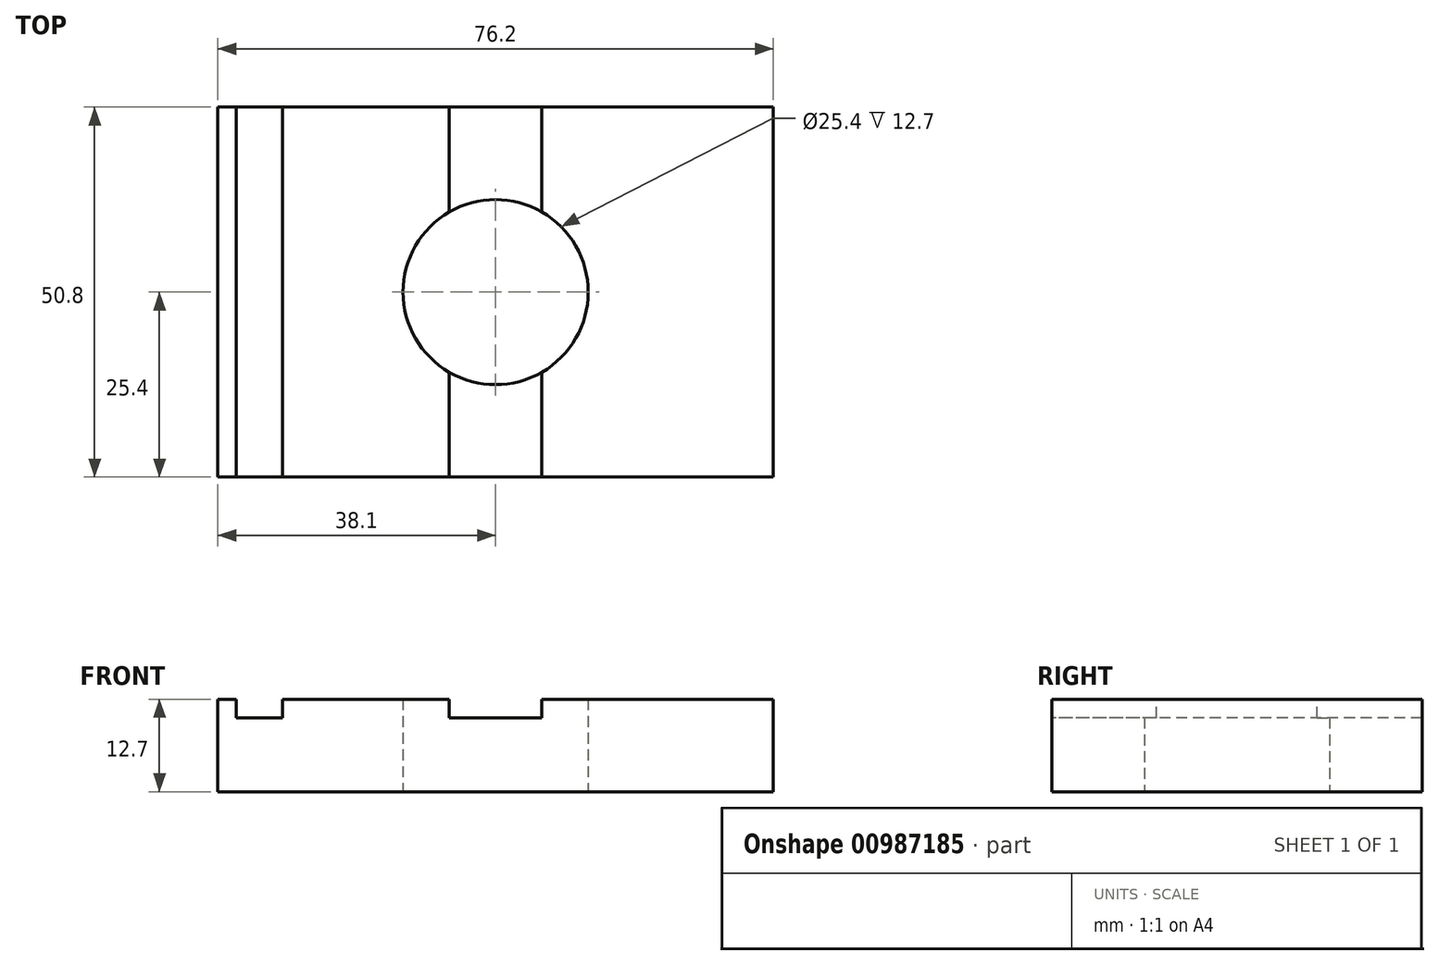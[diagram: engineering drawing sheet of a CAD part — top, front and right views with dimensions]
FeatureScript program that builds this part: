
annotation { "Feature Type Name" : "Feature", "Feature Type Description" : "" }
export const myFeature = defineFeature(function(context is Context, id is Id, definition is map)
    precondition{}
    {
        {
            var Q0;
            Q0=qCreatedBy(makeId("Top.planeOp"),FACE);
            var sketch = newSketch(context, id + "F0", { "sketchPlane" : qUnion([Q0])});
            skLineSegment(sketch, "E0.bottom", {"start": v(-38.1, 25.4) * mm, "end": v(38.1, 25.4) * mm});
            skLineSegment(sketch, "E0.top", {"start": v(-38.1, -25.4) * mm, "end": v(38.1, -25.4) * mm});
            skLineSegment(sketch, "E0.left", {"start": v(-38.1, 25.4) * mm, "end": v(-38.1, -25.4) * mm});
            skLineSegment(sketch, "E0.right", {"start": v(38.1, 25.4) * mm, "end": v(38.1, -25.4) * mm});
            skPoint(sketch, "E0.middle", {"position": v(0, 0) * mm});
            skCircle(sketch, "E1", {"center": v(0, 0) * mm, "radius": 12.7 * mm});
            skSolve(sketch);
        }
        {
            var Q0;
            Q0=makeQuery(id+"F0.imprint","IMPRINT",FACE,{"disambiguationData":[TD([[makeQuery(id+"F0.imprint","IMPRINT",EDGE,{"derivedFrom":sQuery(id+"F0.wireOp",EDGE,"E0.bottom")}),-1.0]])]});
            extrude(context, id + "F1", {"entities" : qUnion([Q0]), "depth" : 12.7 * mm, "offsetDistance" : 25.4 * mm});
        }
        {
            var Q0;
            Q0=makeQuery(id+"F1.opExtrude","CAP_FACE",FACE,{"disambiguationData":[OSD([sQuery(id+"F0.wireOp",EDGE,"E0.bottom"),sQuery(id+"F0.wireOp",EDGE,"E0.top"),sQuery(id+"F0.wireOp",EDGE,"E0.left"),sQuery(id+"F0.wireOp",EDGE,"E0.right"),sQuery(id+"F0.wireOp",EDGE,"E1")])],"isStart":false});
            var sketch = newSketch(context, id + "F2", { "sketchPlane" : qUnion([Q0])});
            skLineSegment(sketch, "E2.bottom", {"start": v(-35.56, 25.4) * mm, "end": v(-29.2, 25.4) * mm});
            skLineSegment(sketch, "E2.top", {"start": v(-35.56, -25.4) * mm, "end": v(-29.2, -25.4) * mm});
            skLineSegment(sketch, "E2.left", {"start": v(-35.56, 25.4) * mm, "end": v(-35.56, -25.4) * mm});
            skLineSegment(sketch, "E2.right", {"start": v(-29.2, 25.4) * mm, "end": v(-29.2, -25.4) * mm});
            skLineSegment(sketch, "E3.bottom", {"start": v(-6.35, 25.4) * mm, "end": v(6.35, 25.4) * mm});
            skLineSegment(sketch, "E3.top", {"start": v(-6.35, -25.4) * mm, "end": v(6.35, -25.4) * mm});
            skLineSegment(sketch, "E3.left", {"start": v(-6.35, 25.4) * mm, "end": v(-6.35, -25.4) * mm});
            skLineSegment(sketch, "E3.right", {"start": v(6.35, 25.4) * mm, "end": v(6.35, -25.4) * mm});
            skPoint(sketch, "E4", {"position": v(0, 0) * mm});
            skPoint(sketch, "E5", {"position": v(0, 25.4) * mm});
            skPoint(sketch, "E6", {"position": v(0, -25.4) * mm});
            skSolve(sketch);
        }
        {
            var Q0;
            Q0=makeQuery(id+"F2.imprint","IMPRINT",FACE,{"disambiguationData":[TD([[makeQuery(id+"F2.imprint","IMPRINT",EDGE,{"derivedFrom":sQuery(id+"F2.wireOp",EDGE,"E2.bottom")}),-1.0]])]});
            var Q1;
            {var subQ0=sQuery(id+"F2.wireOp",EDGE,"E3.bottom");Q1=makeQuery(id+"F2.imprint","IMPRINT",FACE,{"disambiguationData":[TD([[makeQuery(id+"F2.imprint","IMPRINT",EDGE,{"derivedFrom":subQ0}),-1.0]])]});}
            var Q2;
            {var subQ0=sQuery(id+"F2.wireOp",EDGE,"E3.top");Q2=makeQuery(id+"F2.imprint","IMPRINT",FACE,{"disambiguationData":[TD([[makeQuery(id+"F2.imprint","IMPRINT",EDGE,{"derivedFrom":subQ0}),1.0]])]});}
            extrude(context, id + "F3", {"entities" : qUnion([Q0, Q1, Q2]), "operationType" : NewBodyOperationType.REMOVE, "oppositeDirection" : true, "depth" : 2.54 * mm, "offsetDistance" : 25.4 * mm});
        }
    });
